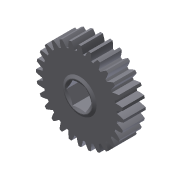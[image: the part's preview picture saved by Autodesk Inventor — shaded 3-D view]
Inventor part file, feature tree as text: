
AUTODESK INVENTOR PART (.ipt)
format: ipt  version: 2011 (Build 150239000, 239)  size: 274,432 bytes
history: native  units: mm (DEFAULTED — no unit token found)
features: sketch x5, extrude x3, plane x3, other x3, chamfer x1, revolve x1, projected_geometry x1
ambient origin geometry x8: Origin, YZ Plane, XZ Plane, XY Plane, X Axis, Y Axis, Z Axis, Center Point
bodies: Solid1 (feature_tree)
feature tree (17):
  extrude  "Extrusion1"  Depth=9.525mm TaperAngle=0.0deg
  plane  "Work Plane1"
  plane  "Work Plane2"
  plane  "Work Plane3"
  other  "Spur Gear"
  extrude  "Extrusion2"  Depth=76.2mm TaperAngle=0.0deg
  extrude  "Extrusion3"  TaperAngle=0.0deg  [1 undecoded]
  chamfer  "Chamfer1"  Distance=49.53mm
  revolve  "Revolution1"  [1 undecoded]
  sketch  "Sketch1"  dims[d0=38.2016mm d1=9.525mm d2=0.0mm]
  sketch  "Sketch2"  dims[d3=35.56mm d4=76.2mm d5=0.0mm]
  other  "Srf1"
  sketch  "Sketch3"  dims[d6=0.0mm d7=1.121997mm d9=0.0mm d14=0.0mm d15=49.53mm]
  sketch  "Sketch4"  dims[d16=0.0mm d17=0.0mm d18=0.0mm d19=49.53mm]
  sketch  "Sketch5"  dims[d20=14.605mm d21=0.635mm d22=0.0mm d23=9.525mm d24=0.0mm d25=0.0mm d26=1.143mm d27=3.175mm d28=26.345745mm d30=1.143mm d31=90.0deg]
  other  "Pitch Diameter"
  projected_geometry  "Project Cut Edges1"
note: 2 required parameter values undecoded (feature->parameter linkage not recoverable at this tier; creation-order binding heuristic only, values carry confidence <= 0.55)